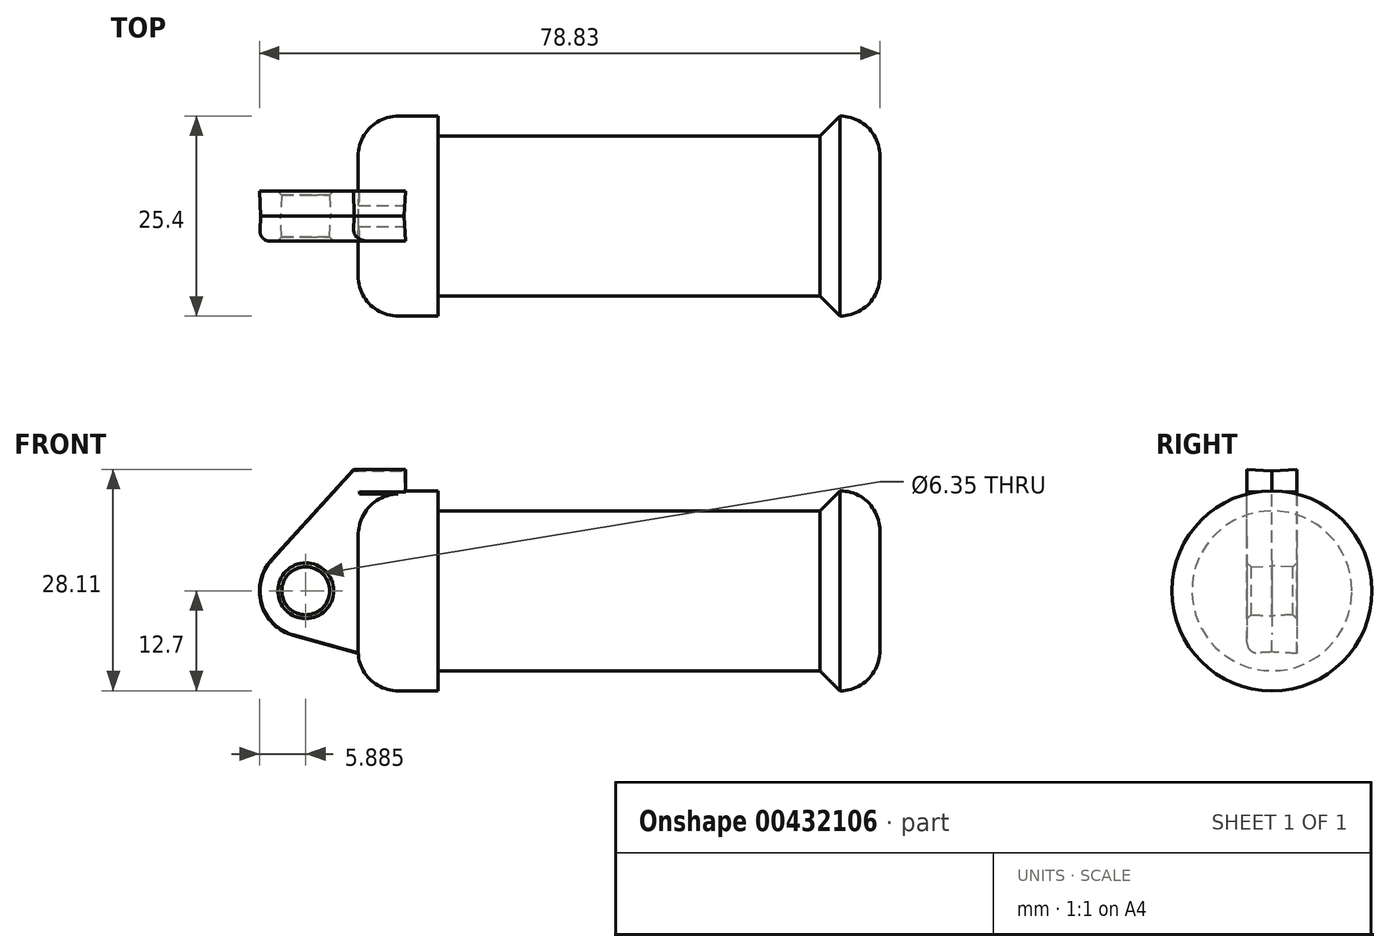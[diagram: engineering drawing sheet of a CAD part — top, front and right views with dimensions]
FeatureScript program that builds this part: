
annotation { "Feature Type Name" : "Feature", "Feature Type Description" : "" }
export const myFeature = defineFeature(function(context is Context, id is Id, definition is map)
    precondition{}
    {
        {
            var Q0;
            Q0=qCreatedBy(makeId("Front.planeOp"),FACE);
            var sketch = newSketch(context, id + "F0", { "sketchPlane" : qUnion([Q0])});
            skLineSegment(sketch, "E0", {"start": v(0, 0) * mm, "end": v(0, 12.7) * mm});
            skLineSegment(sketch, "E1", {"start": v(0, 12.7) * mm, "end": v(10.16, 12.7) * mm});
            skLineSegment(sketch, "E2", {"start": v(10.16, 12.7) * mm, "end": v(10.16, 10.16) * mm});
            skLineSegment(sketch, "E3", {"start": v(10.16, 10.16) * mm, "end": v(56.13, 10.16) * mm});
            skLineSegment(sketch, "E4", {"start": v(56.13, 10.16) * mm, "end": v(56.13, 12.7) * mm});
            skLineSegment(sketch, "E5", {"start": v(56.13, 12.7) * mm, "end": v(66.3, 12.7) * mm});
            skLineSegment(sketch, "E6", {"start": v(66.3, 12.7) * mm, "end": v(66.3, 0) * mm});
            skLineSegment(sketch, "E7", {"start": v(66.3, 0) * mm, "end": v(0, 0) * mm});
            skLineSegment(sketch, "E8", {"start": v(5.84, 15.24) * mm, "end": v(-0.5, 15.24) * mm});
            skLineSegment(sketch, "E9", {"start": v(-0.5, 15.24) * mm, "end": v(-10.88, 3.85) * mm});
            skLineSegment(sketch, "E10", {"start": v(0, 0) * mm, "end": v(-6.65, 0) * mm});
            skCircle(sketch, "E11", {"center": v(-6.65, 0) * mm, "radius": 5.72 * mm});
            skCircle(sketch, "E12", {"center": v(-6.65, 0) * mm, "radius": 3.18 * mm});
            skLineSegment(sketch, "E13", {"start": v(5.84, 15.24) * mm, "end": v(5.84, -9.4) * mm});
            skLineSegment(sketch, "E14", {"start": v(5.84, -9.4) * mm, "end": v(-8.18, -5.5) * mm});
            skSolve(sketch);
        }
        {
            var Q0;
            {var subQ0=sQuery(id+"F0.wireOp",EDGE,"E0");Q0=makeQuery(id+"F0.imprint","IMPRINT",FACE,{"disambiguationData":[TD([[makeQuery(id+"F0.imprint","IMPRINT",EDGE,{"derivedFrom":subQ0}),-1.0]])]});}
            var Q1;
            {var subQ0=sQuery(id+"F0.wireOp",EDGE,"E2");Q1=makeQuery(id+"F0.imprint","IMPRINT",FACE,{"disambiguationData":[TD([[makeQuery(id+"F0.imprint","IMPRINT",EDGE,{"derivedFrom":subQ0}),-1.0]])]});}
            var Q2;
            Q2=sQuery(id+"F0.wireOp",EDGE,"E7");
            revolve(context, id + "F1", {"entities" : qUnion([Q0, Q1]), "axis" : qUnion([Q2]), "revolveType" : RevolveType.FULL});
        }
        {
            var Q0;
            {var subQ1=sQuery(id+"F0.wireOp",EDGE,"E0");Q0=makeQuery(id+"F0.imprint","IMPRINT",FACE,{"disambiguationData":[TD([[makeQuery(id+"F0.imprint","IMPRINT",EDGE,{"derivedFrom":subQ1}),1.0]])]});}
            var Q1;
            {var subQ0=sQuery(id+"F0.wireOp",EDGE,"E14");Q1=makeQuery(id+"F0.imprint","IMPRINT",FACE,{"disambiguationData":[TD([[makeQuery(id+"F0.imprint","IMPRINT",EDGE,{"derivedFrom":subQ0}),-1.0]])]});}
            var Q2;
            {var subQ5=sQuery(id+"F0.wireOp",EDGE,"E12");Q2=makeQuery(id+"F0.imprint","IMPRINT",FACE,{"disambiguationData":[TD([[makeQuery(id+"F0.imprint","IMPRINT",EDGE,{"derivedFrom":subQ5}),-1.0]])]});}
            extrude(context, id + "F2", {"entities" : qUnion([Q0, Q1, Q2]), "operationType" : NewBodyOperationType.ADD, "endBound" : BoundingType.SYMMETRIC, "depth" : 6.35 * mm, "hasDraft" : true, "draftAngle" : 3 * degree});
        }
        {
            var Q0;
            Q0=makeQuery(id+"F1.opRevolve","SWEPT_EDGE",EDGE,{"disambiguationData":[OSD([sQuery(id+"F0.wireOp",EDGE,"E5"),sQuery(id+"F0.wireOp",EDGE,"E6")])]});
            fillet(context, id + "F3", {"entities" : qUnion([Q0]), "radius" : 5.08 * mm, "tangentPropagation" : true, "allowEdgeOverflow" : false});
        }
        {
            var Q0;
            Q0=makeQuery(id+"F1.opRevolve","SWEPT_EDGE",EDGE,{"disambiguationData":[OSD([sQuery(id+"F0.wireOp",EDGE,"E4"),sQuery(id+"F0.wireOp",EDGE,"E5")])]});
            chamfer(context, id + "F4", {"entities" : qUnion([Q0]), "width" : 5.08 * mm, "tangentPropagation" : true});
        }
        {
            var Q0;
            Q0=makeQuery(id+"F1.opRevolve","SWEPT_EDGE",EDGE,{"disambiguationData":[OSD([sQuery(id+"F0.wireOp",EDGE,"E0"),sQuery(id+"F0.wireOp",EDGE,"E1")])]});
            fillet(context, id + "F5", {"entities" : qUnion([Q0]), "radius" : 5.08 * mm, "tangentPropagation" : true, "allowEdgeOverflow" : false});
        }
        {
            var Q0;
            Q0=makeQuery(id+"F2.opExtrude","CAP_EDGE",EDGE,{"disambiguationData":[OSD([sQuery(id+"F0.wireOp",EDGE,"E9")])],"isStart":false});
            var Q1;
            Q1=makeQuery(id+"F2.opExtrude","CAP_EDGE",EDGE,{"disambiguationData":[OSD([sQuery(id+"F0.wireOp",EDGE,"E11")])],"isStart":false});
            var Q2;
            Q2=makeQuery(id+"F2.opExtrude","CAP_EDGE",EDGE,{"disambiguationData":[OSD([sQuery(id+"F0.wireOp",EDGE,"E14")])],"isStart":false});
            fillet(context, id + "F6", {"entities" : qUnion([Q0, Q1, Q2]), "radius" : 1.27 * mm, "tangentPropagation" : true, "allowEdgeOverflow" : false});
        }
        {
            var Q0;
            Q0=makeQuery(id+"F2.*.split.splitOp","SPLIT",FACE,{"derivedFrom":makeQuery(id+"F2.opExtrude","SWEPT_FACE",FACE,{"disambiguationData":[OSD([sQuery(id+"F0.wireOp",EDGE,"E12")])]})});
            var Q1;
            Q1=makeQuery(id+"F2.*.split.splitOp","SPLIT",FACE,{"derivedFrom":makeQuery(id+"F2.opExtrude","SWEPT_FACE",FACE,{"disambiguationData":[OSD([sQuery(id+"F0.wireOp",EDGE,"E12")])]}),"isFromBackBody":true});
            chamfer(context, id + "F7", {"entities" : qUnion([Q0, Q1]), "width" : 0.5 * mm, "tangentPropagation" : true});
        }
    });
